# Revit family: MONO TREND_85x85x2
name_source: partatom
category: Plumbing Fixtures
revit_build: Autodesk Revit 2018 (Build: 20170223_1515(x64)
units: mm (PartAtom-declared; Revit-internal decimal feet)

## family parameters
Always vertical = Yes
Cut with Voids When Loaded = No
OmniClass Number = 23.45.00.00
OmniClass Title = Sanitary, Laundry, and Cleaning Equipment
Part Type = Normal
Room Calculation Point = No
Round Connector Dimension = Use Diameter
Shared = No
Work Plane-Based = Yes

## types (1)
- Pneumatique_Inox chromé
    BIM object developer = www.concepsysbim.com
    CONTROL_Actuation type = Pneumatique
    CONTROL_Brief description = Plaque de commande simple débit. Anti-vandalisme
    CONTROL_Height = 85 mm  [stored 0.278871 ft]
    CONTROL_Length = 85 mm  [stored 0.278871 ft]
    CONTROL_Material = Inox chromé
    CONTROL_Model = MONO TREND
    CONTROL_Model Series = Inox chromé
    CONTROL_Model code/ref = 1628IC
    CONTROL_Product data url = https://www.regiplast.fr
    CONTROL_Type of flush = Simple-Débit
    CONTROL_Type/function = Plaque de Commande pour réservoir à encastrer
    CONTROL_Vandal-proof = Oui
    CONTROL_Width = 2 mm  [stored 0.00656168 ft]
    Default Elevation = 1219.2 mm  [stored 4 ft]
    Description = Plaque de commande simple débit. Anti-vandalisme
    Model = MONO TREND
    Product data url = https://www.regiplast.fr
    URL = https://www.regiplast.fr

note: [stored X ft] marks values corroborated as IEEE doubles in the binary element streams (Revit-internal decimal feet)

## geometry (parser evidence)
native form markers: Sweep x2
no freeform markers — native parametric forms only
